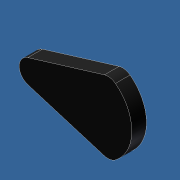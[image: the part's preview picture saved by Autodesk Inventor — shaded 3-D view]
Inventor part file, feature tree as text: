
AUTODESK INVENTOR PART (.ipt)
format: ipt  version: unknown  size: 200,192 bytes
history: native  units: in
note: dims shown in document units (in); Inventor stores cm internally (conversion verified against a paired STEP export)
features: extrude x4, sketch x4
ambient origin geometry x8: Origin, YZ Plane, XZ Plane, XY Plane, X Axis, Y Axis, Z Axis, Center Point
bodies: Solid1 (feature_tree)
feature tree (8):
  extrude  "Extrusion1"  Depth=0.05in TaperAngle=0.0deg
  extrude  "Extrusion2"  Depth=0.05in TaperAngle=0.0deg
  extrude  "Extrusion3"  Depth=0.05in TaperAngle=0.0deg
  extrude  "Extrusion4"  Depth=0.375in
  sketch  "Sketch1"  dims[d0=0.35in d1=0.05in d2=0.0in]
  sketch  "Sketch2"  dims[d3=0.1in d4=0.05in d5=0.0in]
  sketch  "Sketch3"  dims[d6=0.25in d7=0.05in d8=0.0in]
  sketch  "Sketch4"  dims[d9=0.75in d13=0.375in d14=0.25in d15=0.425in d16=0.125in d17=0.15in d18=0.0in d20=0.0in d21=0.875in d22=0.125in]
